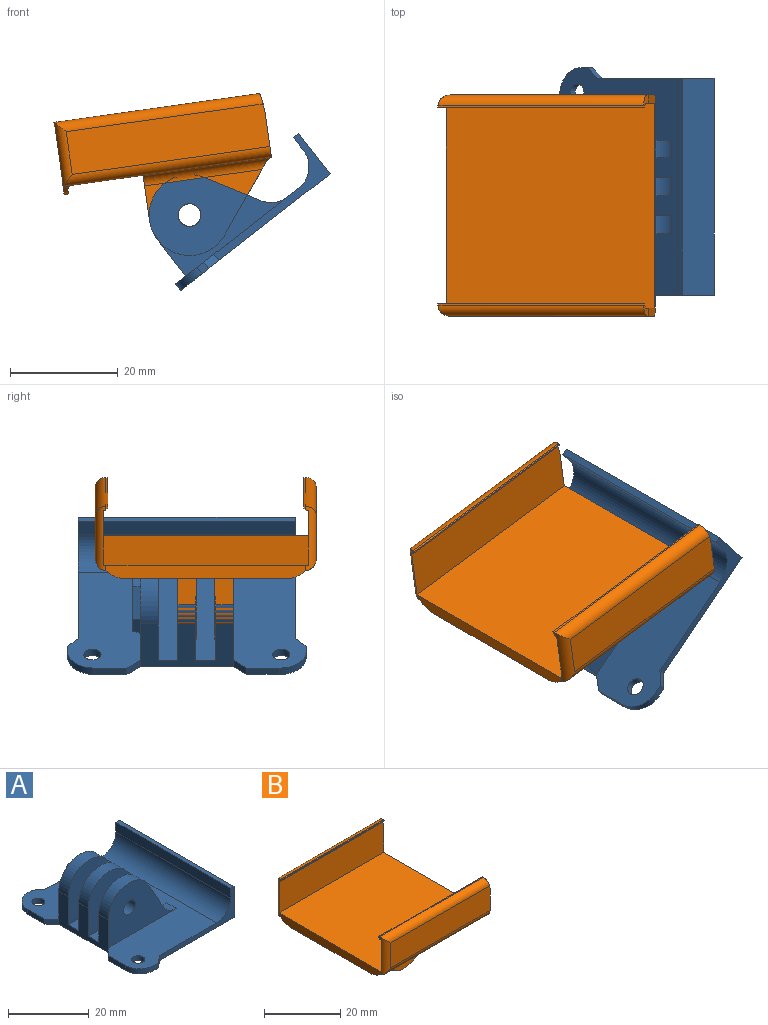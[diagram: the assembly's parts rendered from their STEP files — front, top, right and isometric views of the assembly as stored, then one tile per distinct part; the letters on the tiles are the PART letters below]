
ASSEMBLY  parts=2 mates=1
PART A: 54 faces, bbox 35.1x44.2x17.5 mm
  f0: plane 23.87x16mm, normal (0,1,0), area 149.7mm2, adj f6,f7,f27,f35,f38,f46,f47,f48
  f1: cylinder r=2.1mm len=4.2mm, axis (0,-1,0), area 22.4mm2, adj f3,f45
  f2: plane 23.87x16mm, normal (0,1,0), area 234.9mm2, adj f6,f7,f28,f29,f33,f36
  f3: plane 23.87x16mm, normal (0,-1,0), area 234.9mm2, adj f1,f6,f7,f27,f35,f38
  f4: plane 23.87x16mm, normal (0,1,0), area 234.9mm2, adj f6,f7,f25,f26,f34,f37
  f5: plane 23.87x16mm, normal (0,-1,0), area 234.9mm2, adj f6,f7,f25,f26,f34,f37
  f6: plane 44.2x28.9mm, normal (0,0,1), area 882.4mm2, adj f0,f2,f3,f4,f5,f7,f8,f9
  f7: plane 17.3x10mm, normal (-1,0,0), area 110.1mm2, adj f0,f2,f3,f4,f5,f6,f8,f19
  f8: plane 2.45x2.4mm, normal (-0.71,0.7,0), area 5.1mm2, adj f6,f7,f9,f21
  f9: plane 6x1.5mm, normal (-1,0,0), area 9mm2, adj f6,f8,f21,f31
  f10: plane 1.6x1.5mm, normal (0,-1,0), area 2.4mm2, adj f6,f11,f21,f31
  f11: plane 2.38x2mm, normal (0.64,-0.77,0), area 4.7mm2, adj f6,f10,f12,f21
  f12: plane 26.12x9.5mm, normal (0,-1,0), area 54.1mm2, adj f6,f11,f13,f21,f22,f23,f32
  f13: plane 40.2x9.5mm, normal (1,0,0), area 381.9mm2, adj f12,f14,f21,f23
  f14: plane 26.12x9.5mm, normal (0,1,0), area 54.1mm2, adj f6,f13,f15,f21,f22,f23,f32
  f15: plane 2.38x2mm, normal (0.64,0.77,0), area 4.7mm2, adj f6,f14,f16,f21
  f16: plane 1.6x1.5mm, normal (0,1,0), area 2.4mm2, adj f6,f15,f21,f30
  f17: plane 6x1.5mm, normal (-1,0,0), area 9mm2, adj f6,f19,f21,f30
  f18: cylinder r=1.6mm len=3.2mm, axis (0,0,1), area 15.1mm2, adj f6,f21
  f19: plane 2.45x2.4mm, normal (-0.71,-0.7,0), area 5.1mm2, adj f6,f7,f17,f21
  f20: cylinder r=1.6mm len=3.2mm, axis (0,0,1), area 15.1mm2, adj f6,f21
  f21: plane 44.2x35.1mm, normal (0,0,-1), area 1368mm2, adj f7,f8,f9,f10,f11,f12,f13,f14
  f22: plane 40.2x3mm, normal (-1,0,0), area 120.6mm2, adj f12,f14,f23,f32
  f23: plane 40.2x1.2mm, normal (0,0,1), area 48.2mm2, adj f12,f13,f14,f22
  f24: plane 23.87x16mm, normal (0,-1,0), area 234.9mm2, adj f6,f7,f28,f29,f33,f36
  f25: cylinder r=2.1mm len=4.2mm, axis (0,-1,0), area 43.5mm2, adj f4,f5
  f26: cylinder r=7.5mm len=14.24mm, axis (0,-1,0), area 66.5mm2, adj f4,f5,f7,f34
  f27: cylinder r=7.5mm len=14.24mm, axis (0,-1,0), area 66.5mm2, adj f0,f3,f7,f35
  f28: cylinder r=2.1mm len=4.2mm, axis (0,-1,0), area 43.5mm2, adj f2,f24
  f29: cylinder r=7.5mm len=14.24mm, axis (0,-1,0), area 66.5mm2, adj f2,f7,f24,f33
  f30: cylinder r=5mm len=5mm, axis (0,0,-1), area 11.8mm2, adj f6,f16,f17,f21
  f31: cylinder r=5mm len=5mm, axis (0,0,1), area 11.8mm2, adj f6,f9,f10,f21
  f32: cylinder r=5mm len=40.2mm, axis (0,-1,0), area 315.7mm2, adj f6,f12,f14,f22
  f33: plane 9.28x5.3mm, normal (0.87,0,0.5), area 35.3mm2, adj f2,f24,f29,f36
  f34: plane 9.28x5.3mm, normal (0.87,0,0.5), area 35.3mm2, adj f4,f5,f26,f37
  f35: plane 9.28x5.3mm, normal (0.87,0,0.5), area 35.3mm2, adj f0,f3,f27,f38
  f36: cylinder r=5mm len=4.34mm, axis (0,1,0), area 17.4mm2, adj f2,f6,f24,f33
  f37: cylinder r=5mm len=4.34mm, axis (0,1,0), area 17.4mm2, adj f4,f5,f6,f34
  f38: cylinder r=5mm len=4.34mm, axis (0,-1,0), area 17.4mm2, adj f0,f3,f6,f35
  f39: plane 3.7x3mm, normal (0.87,0,0.5), area 12.8mm2, adj f40,f44,f45,f52
  f40: plane 3.7x3mm, normal (0.87,0,-0.5), area 12.8mm2, adj f39,f41,f45,f52
  f41: plane 4.27x3mm, normal (0,0,-1), area 12.8mm2, adj f40,f42,f45,f52
  f42: plane 3.7x3mm, normal (-0.87,0,-0.5), area 12.8mm2, adj f41,f43,f45,f52
  f43: plane 3.7x3mm, normal (-0.87,0,0.5), area 12.8mm2, adj f42,f44,f45,f52
  f44: plane 4.27x3mm, normal (0,0,1), area 12.8mm2, adj f39,f43,f45,f52
  f45: plane 8.54x7.4mm, normal (0,1,0), area 33.6mm2, adj f1,f39,f40,f41,f42,f43,f44
  f46: plane 6x1.4mm, normal (0,0,1), area 8.4mm2, adj f0,f47,f51,f52
  f47: plane 5.2x3mm, normal (0.87,0,0.5), area 8.4mm2, adj f0,f46,f48,f52
  f48: plane 6.2x3.58mm, normal (0.87,0,-0.5), area 9mm2, adj f0,f47,f49,f52,f53
  f49: plane 6x0.4mm, normal (0,0,-1), area 2.4mm2, adj f48,f50,f52,f53
  f50: plane 6.2x3.58mm, normal (-0.87,0,-0.5), area 9mm2, adj f0,f49,f51,f52,f53
  f51: plane 5.2x3mm, normal (-0.87,0,0.5), area 8.4mm2, adj f0,f46,f50,f52
  f52: plane 12.01x10.4mm, normal (0,1,0), area 46.2mm2, adj f39,f40,f41,f42,f43,f44,f46,f47
  f53: plane 6x1mm, normal (0,0.71,-0.71), area 7.7mm2, adj f0,f48,f49,f50
PART B: 47 faces, bbox 39.1x41.1x28.1 mm
  f0: plane 38.5x0.3mm, normal (0,0,1), area 11.6mm2, adj f1,f19,f31,f33
  f1: plane 3x2.3mm, normal (0.99,0,0.16), area 4.2mm2, adj f0,f10,f11,f14,f18,f19,f21,f33
  f2: plane 37x2.5mm, normal (-1,0,0), area 89.2mm2, adj f13,f34,f37,f43,f45,f46
  f3: plane 0.6x0.3mm, normal (-1,0,0), area 0.1mm2, adj f15,f17,f20,f37
  f4: plane 37x8mm, normal (0,1,0), area 295.9mm2, adj f11,f28,f35,f36,f37
  f5: plane 24x16mm, normal (0,1,0), area 249.3mm2, adj f12,f23,f25,f26,f30,f41
  f6: plane 21.94x14mm, normal (0,1,0), area 203.7mm2, adj f8,f24,f27,f29,f38
  f7: plane 24x16mm, normal (0,-1,0), area 249.3mm2, adj f8,f12,f24,f27,f29,f39
  f8: plane 8.5x5.5mm, normal (-1,0,0), area 30.6mm2, adj f6,f7,f12,f24,f38
  f9: plane 38.94x10.2mm, normal (0,-1,0), area 396.7mm2, adj f11,f13,f16,f28,f37
  f10: plane 37x8mm, normal (0,-1,0), area 295.9mm2, adj f1,f11,f32,f33,f34
  f11: plane 41x9mm, normal (1,0,0), area 63.3mm2, adj f1,f4,f9,f10,f12,f13,f14,f28
  f12: plane 37.4x37mm, normal (0,0,-1), area 1119.8mm2, adj f5,f7,f8,f11,f23,f32,f36,f38
  f13: plane 39x38mm, normal (0,0,1), area 1482mm2, adj f2,f9,f11,f14,f34,f37
  f14: plane 38.94x10.2mm, normal (0,1,0), area 396.7mm2, adj f1,f11,f13,f18,f34
  f15: plane 38.5x0.3mm, normal (0,0,1), area 11.5mm2, adj f3,f17,f28,f35
  f16: plane 38.62x0.3mm, normal (0,0,-1), area 11.6mm2, adj f9,f20,f28,f37
  f17: plane 38.55x0.3mm, normal (0,-1,0), area 11.6mm2, adj f3,f15,f20,f28
  f18: plane 38.62x0.3mm, normal (0,0,-1), area 11.6mm2, adj f1,f14,f21,f34
  f19: plane 38.55x0.3mm, normal (0,1,0), area 11.6mm2, adj f0,f1,f21,f31
  f20: plane 38.63x0.5mm, normal (0,-0.71,-0.71), area 27.3mm2, adj f3,f16,f17,f28,f37
  f21: plane 38.63x0.5mm, normal (0,0.71,-0.71), area 27.3mm2, adj f1,f18,f19,f31,f34
  f22: plane 21.94x14mm, normal (0,-1,0), area 203.7mm2, adj f23,f25,f26,f30,f40
  f23: plane 8.5x5.5mm, normal (-1,0,0), area 30.6mm2, adj f5,f12,f22,f25,f40
  f24: cylinder r=7.5mm len=13.95mm, axis (0,-1,0), area 68.4mm2, adj f6,f7,f8,f29
  f25: cylinder r=7.5mm len=13.95mm, axis (0,-1,0), area 68.4mm2, adj f5,f22,f23,f30
  f26: cylinder r=2.1mm len=4.2mm, axis (0,-1,0), area 46.2mm2, adj f5,f22
  f27: cylinder r=2.1mm len=4.2mm, axis (0,-1,0), area 46.2mm2, adj f6,f7
  f28: plane 3x2.3mm, normal (0.99,0,0.16), area 4.2mm2, adj f4,f9,f11,f15,f16,f17,f20,f35
  f29: plane 11.69x9.06mm, normal (0.79,0,-0.61), area 51.7mm2, adj f6,f7,f24,f38,f39
  f30: plane 11.69x9.06mm, normal (0.79,0,-0.61), area 51.7mm2, adj f5,f22,f25,f40,f41
  f31: plane 0.6x0.3mm, normal (-1,0,0), area 0.1mm2, adj f0,f19,f21,f34
  f32: cylinder r=2mm len=39mm, axis (-1,0,0), area 120.2mm2, adj f10,f11,f12,f34,f46
  f33: cylinder r=2mm len=38.83mm, axis (1,0,0), area 119mm2, adj f0,f1,f10,f34
  f34: cylinder r=2mm len=12mm, axis (0,0,-1), area 28mm2, adj f2,f10,f13,f14,f18,f21,f31,f32
  f35: cylinder r=2mm len=38.83mm, axis (-1,0,0), area 119mm2, adj f4,f15,f28,f37
  f36: cylinder r=2mm len=39mm, axis (1,0,0), area 120.2mm2, adj f4,f11,f12,f37,f45
  f37: cylinder r=2mm len=12mm, axis (0,0,-1), area 28mm2, adj f2,f3,f4,f9,f13,f16,f20,f35
  f38: cylinder r=2mm len=24mm, axis (-1,0,0), area 72.4mm2, adj f6,f8,f12,f29,f39
  f39: cylinder r=2mm len=5.5mm, axis (0,-1,0), area 5.9mm2, adj f7,f11,f29,f38
  f40: cylinder r=2mm len=24mm, axis (1,0,0), area 72.4mm2, adj f12,f22,f23,f30,f41
  f41: cylinder r=2mm len=5.5mm, axis (0,-1,0), area 5.9mm2, adj f5,f11,f30,f40
  f42: plane 34.96x0.7mm, normal (1,0,0), area 23.3mm2, adj f43,f44,f45,f46
  f43: plane 29.86x0.8mm, normal (0,0,-1), area 23.9mm2, adj f2,f42,f45,f46
  f44: cylinder r=0.8mm len=37mm, axis (0,1,0), area 45.7mm2, adj f12,f42,f45,f46
  f45: cylinder r=5mm len=3.57mm, axis (1,0,0), area 3.4mm2, adj f2,f36,f42,f43,f44
  f46: cylinder r=5mm len=3.57mm, axis (-1,0,0), area 3.4mm2, adj f2,f32,f42,f43,f44
PLACE A rot(axis=(0,-1,0),38deg) t=(-18,15.08,-14.85)mm
PLACE B rot(axis=(0,-1,0),8deg) t=(-21.99,15.27,4.55)mm
MATE revolute B.f24 <-> A.f1  axis (0,-1,0) through (-18.66,6.43,-4.58)mm
